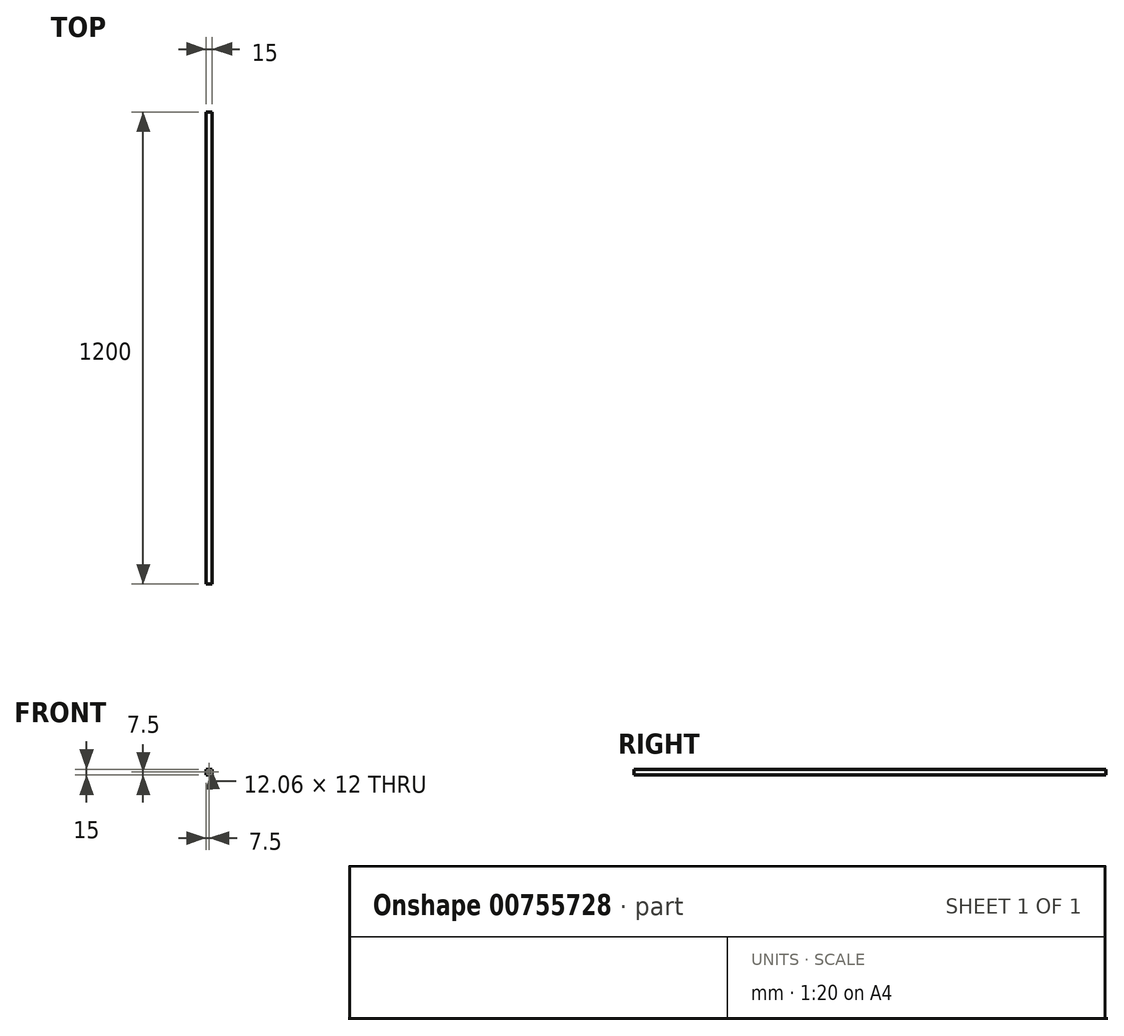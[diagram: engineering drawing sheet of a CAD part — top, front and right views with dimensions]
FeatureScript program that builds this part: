
annotation { "Feature Type Name" : "Feature", "Feature Type Description" : "" }
export const myFeature = defineFeature(function(context is Context, id is Id, definition is map)
    precondition{}
    {
        {
            assignVariable(context, id + "F0", {"name" : "l", "anyValue" : 1200});
        }
        {
            var Q0;
            Q0=qCreatedBy(makeId("Front.planeOp"),FACE);
            var sketch = newSketch(context, id + "F1", { "sketchPlane" : qUnion([Q0])});
            skLineSegment(sketch, "E0.bottom", {"start": v(0, 0) * mm, "end": v(15, 0) * mm});
            skLineSegment(sketch, "E0.top", {"start": v(0, 15) * mm, "end": v(15, 15) * mm});
            skLineSegment(sketch, "E0.left", {"start": v(0, 0) * mm, "end": v(0, 15) * mm});
            skLineSegment(sketch, "E0.right", {"start": v(15, 0) * mm, "end": v(15, 15) * mm});
            skLineSegment(sketch, "E1", {"start": v(0, 15) * mm, "end": v(15, 0) * mm, "construction": true});
            skLineSegment(sketch, "E2", {"start": v(0, 0) * mm, "end": v(15, 15) * mm, "construction": true});
            skPoint(sketch, "E3", {"position": v(7.5, 7.5) * mm});
            skLineSegment(sketch, "E4.bottom", {"start": v(13.53, 13.5) * mm, "end": v(1.47, 13.5) * mm});
            skLineSegment(sketch, "E4.top", {"start": v(13.53, 1.5) * mm, "end": v(1.47, 1.5) * mm});
            skLineSegment(sketch, "E4.left", {"start": v(13.53, 13.5) * mm, "end": v(13.53, 1.5) * mm});
            skLineSegment(sketch, "E4.right", {"start": v(1.47, 13.5) * mm, "end": v(1.47, 1.5) * mm});
            skSolve(sketch);
        }
        {
            var Q0;
            Q0=makeQuery(id+"F1.imprint","IMPRINT",FACE,{"disambiguationData":[TD([[makeQuery(id+"F1.imprint","IMPRINT",EDGE,{"derivedFrom":sQuery(id+"F1.wireOp",EDGE,"E0.bottom")}),1.0]])]});
            extrude(context, id + "F2", {"entities" : qUnion([Q0]), "depth" : getVariable(context, 'l') * mm, "offsetDistance" : 25 * mm});
        }
    });
